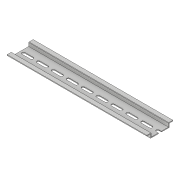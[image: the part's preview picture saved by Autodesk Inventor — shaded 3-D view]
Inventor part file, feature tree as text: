
AUTODESK INVENTOR PART (.ipt)
format: ipt  version: 2022 (Build 260153000, 153)  size: 206,336 bytes
history: native  units: in
note: dims shown in document units (in); Inventor stores cm internally (conversion verified against a paired STEP export)
features: extrude x1, sketch x1, imported_body x1
ambient origin geometry x8: Origin, YZ Plane, XZ Plane, XY Plane, X Axis, Y Axis, Z Axis, Center Point
bodies: Solid1 (feature_tree)
feature tree (3):
  extrude  "Extrusion1"  [1 undecoded]
  sketch  "Sketch1"  dims[d0=31.9882in d1=0.0in]
  imported_body  "Base1"
note: 1 required parameter value undecoded (feature->parameter linkage not recoverable at this tier; creation-order binding heuristic only, values carry confidence <= 0.55)
